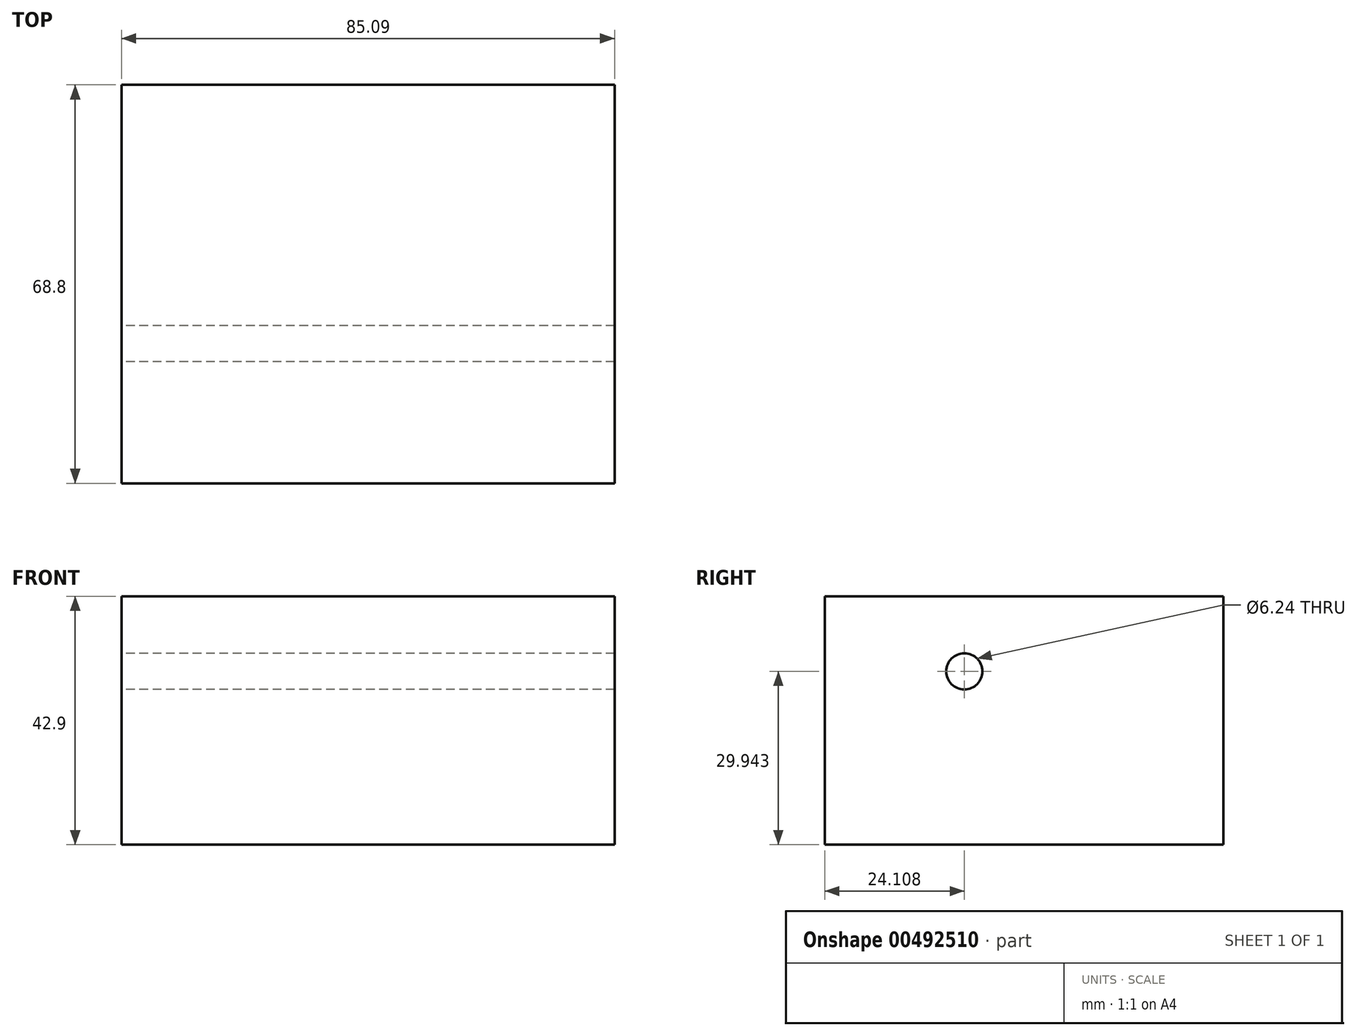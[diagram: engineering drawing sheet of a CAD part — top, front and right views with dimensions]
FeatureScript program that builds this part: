
annotation { "Feature Type Name" : "Feature", "Feature Type Description" : "" }
export const myFeature = defineFeature(function(context is Context, id is Id, definition is map)
    precondition{}
    {
        {
            var Q0;
            Q0=qCreatedBy(makeId("Right.planeOp"),FACE);
            var sketch = newSketch(context, id + "F0", { "sketchPlane" : qUnion([Q0])});
            skLineSegment(sketch, "E0.bottom", {"start": v(-79.37, 57.4) * mm, "end": v(-10.57, 57.4) * mm});
            skLineSegment(sketch, "E0.top", {"start": v(-79.37, 14.51) * mm, "end": v(-10.57, 14.51) * mm});
            skLineSegment(sketch, "E0.left", {"start": v(-79.37, 57.4) * mm, "end": v(-79.37, 14.51) * mm});
            skLineSegment(sketch, "E0.right", {"start": v(-10.57, 57.4) * mm, "end": v(-10.57, 14.51) * mm});
            skCircle(sketch, "E1", {"center": v(-55.26, 44.45) * mm, "radius": 3.12 * mm});
            skSolve(sketch);
        }
        {
            var Q0;
            Q0=makeQuery(id+"F0.imprint","IMPRINT",FACE,{"disambiguationData":[TD([[makeQuery(id+"F0.imprint","IMPRINT",EDGE,{"derivedFrom":sQuery(id+"F0.wireOp",EDGE,"E0.bottom")}),-1.0]])]});
            var Q1;
            Q1=sQuery(id+"F0.wireOp",EDGE,"E0.bottom");
            extrude(context, id + "F1", {"entities" : qUnion([Q0]), "surfaceEntities" : qUnion([Q1]), "depth" : 85.1 * mm});
        }
    });
